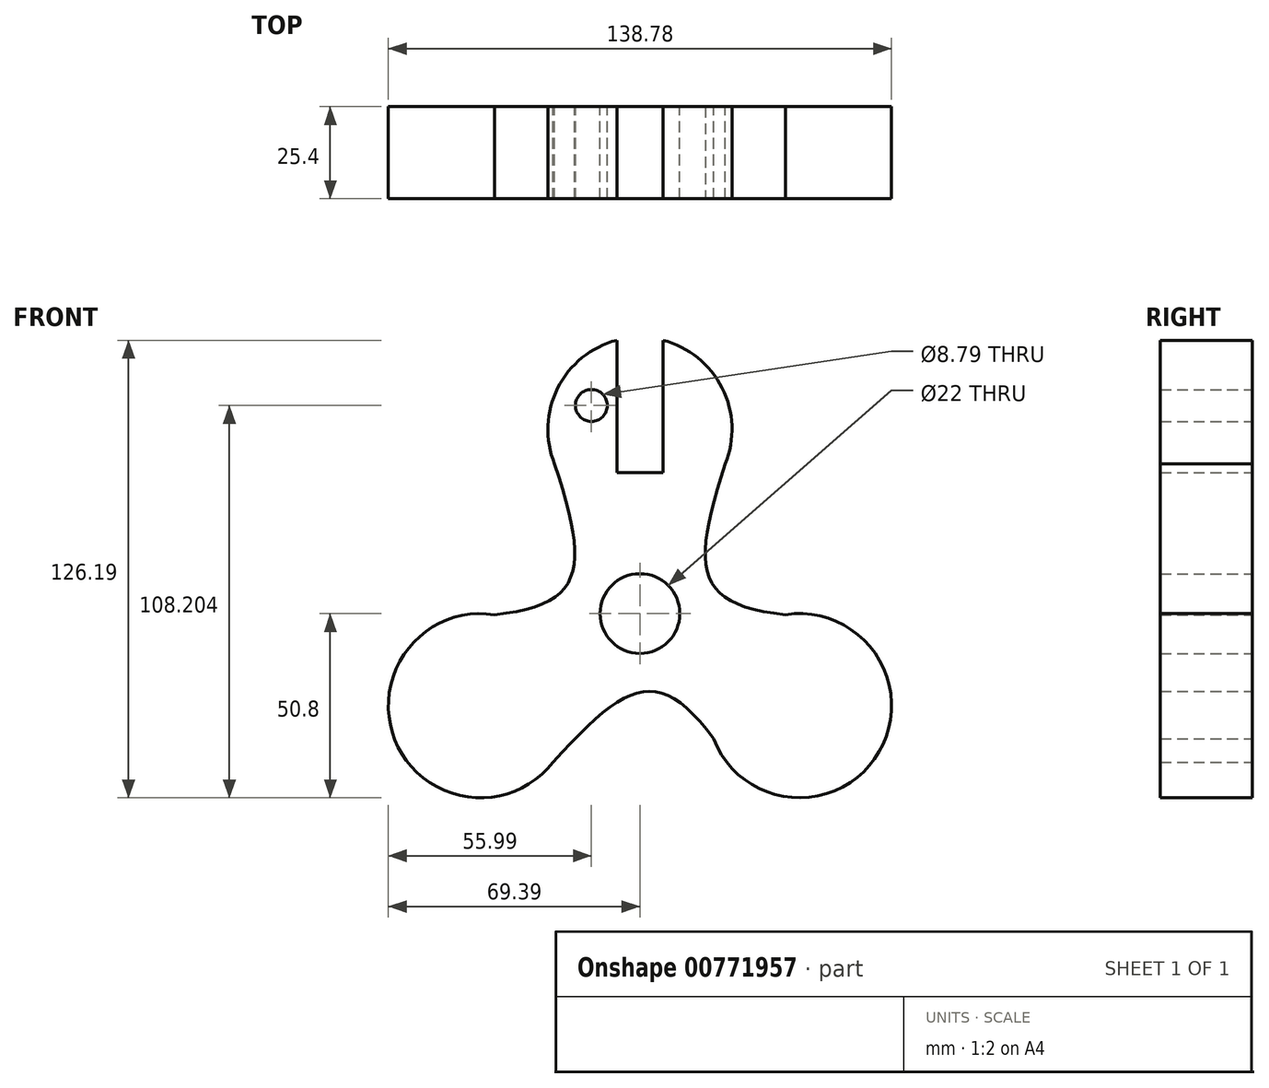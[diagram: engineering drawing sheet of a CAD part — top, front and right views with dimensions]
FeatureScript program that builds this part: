
annotation { "Feature Type Name" : "Feature", "Feature Type Description" : "" }
export const myFeature = defineFeature(function(context is Context, id is Id, definition is map)
    precondition{}
    {
        {
            var Q0;
            Q0=qCreatedBy(makeId("Front.planeOp"),FACE);
            var sketch = newSketch(context, id + "F0", { "sketchPlane" : qUnion([Q0])});
            skCircle(sketch, "E0", {"center": v(0, 0) * mm, "radius": 50.8 * mm, "construction": true});
            skCircle(sketch, "E1", {"center": v(0, 0) * mm, "radius": 11 * mm});
            skLineSegment(sketch, "E2", {"start": v(0, 0) * mm, "end": v(0, 50.8) * mm, "construction": true});
            skLineSegment(sketch, "E3", {"start": v(0, 0) * mm, "end": v(-44, -25.4) * mm, "construction": true});
            skLineSegment(sketch, "E4", {"start": v(0, 0) * mm, "end": v(44, -25.4) * mm, "construction": true});
            skArc(sketch, "E5", {"start": v(-6.35, 75.4) * mm, "mid": v(0, 25.4) * mm, "end": v(6.35, 75.4) * mm});
            skPoint(sketch, "E6.center", {"position": v(-0.18, 4.76) * mm});
            skLineSegment(sketch, "E7", {"start": v(0, 0) * mm, "end": v(38.5, 22.22) * mm, "construction": true});
            skLineSegment(sketch, "E8", {"start": v(0, 0) * mm, "end": v(0, -44.45) * mm, "construction": true});
            skLineSegment(sketch, "E9", {"start": v(0, 0) * mm, "end": v(-38.5, 22.22) * mm, "construction": true});
            skCircle(sketch, "E10", {"center": v(44, -25.4) * mm, "radius": 25.4 * mm});
            skCircle(sketch, "E11", {"center": v(-44, -25.4) * mm, "radius": 25.4 * mm});
            skLineSegment(sketch, "E12", {"start": v(-6.35, 75.4) * mm, "end": v(-6.35, 38.84) * mm});
            skLineSegment(sketch, "E13", {"start": v(0, 50.8) * mm, "end": v(0, 76.2) * mm, "construction": true});
            skLineSegment(sketch, "E14", {"start": v(6.35, 38.84) * mm, "end": v(6.35, 75.4) * mm});
            skLineSegment(sketch, "E15", {"start": v(-6.35, 38.84) * mm, "end": v(6.35, 38.84) * mm});
            skPoint(sketch, "E16.visualSharp", {"position": v(-38.5, 22.22) * mm});
            skPoint(sketch, "E17.visualSharp", {"position": v(38.5, 22.22) * mm});
            skPoint(sketch, "E18.visualSharp", {"position": v(0, -44.45) * mm});
            skLineSegment(sketch, "E19", {"start": v(-50.8, -0.93) * mm, "end": v(-50.8, -0.93) * mm});
            skLineSegment(sketch, "E20.2.0", {"start": v(24.6, 44.45) * mm, "end": v(24.6, 44.45) * mm});
            skArc(sketch, "E20.2.1", {"start": v(-24.6, 44.45) * mm, "mid": v(-23.62, 41.6) * mm, "end": v(-22.4, 38.84) * mm});
            skPoint(sketch, "E21", {"position": v(44, 0) * mm});
            skPoint(sketch, "E22.1.0", {"position": v(-22, 38.1) * mm});
            skPoint(sketch, "E22.2.0", {"position": v(-22, -38.1) * mm});
            skPoint(sketch, "E23", {"position": v(-50.8, -0.93) * mm});
            skPoint(sketch, "E24", {"position": v(24.6, 44.45) * mm});
            skPoint(sketch, "E25", {"position": v(26.2, -43.52) * mm});
            skPoint(sketch, "E26.start.orphan", {"position": v(55.46, 0) * mm});
            skPoint(sketch, "E27", {"position": v(-26.2, -43.52) * mm});
            skPoint(sketch, "E28.1.0", {"position": v(50.8, -0.93) * mm});
            skPoint(sketch, "E28.2.0", {"position": v(-24.6, 44.45) * mm});
            skLineSegment(sketch, "E29", {"start": v(-22, -12.7) * mm, "end": v(22, -12.7) * mm, "construction": true});
            skLineSegment(sketch, "E30", {"start": v(22, -12.7) * mm, "end": v(0, 25.4) * mm, "construction": true});
            skLineSegment(sketch, "E31", {"start": v(0, 25.4) * mm, "end": v(-22, -12.7) * mm, "construction": true});
            skFitSpline(sketch, "E32", {"points": [v(-26.2, -43.52) * mm, v(26.2, -43.52) * mm], "startDerivative": vector(72.18, 81.54) * mm, "endDerivative": vector(58.11, -95.1) * mm});
            skFitSpline(sketch, "E33.MirrorCS", {"points": [v(24.6, 44.45) * mm, v(50.8, -0.93) * mm], "startDerivative": vector(-34.52, -103.28) * mm, "endDerivative": vector(111.41, -2.78) * mm});
            skFitSpline(sketch, "E34.MirrorCS", {"points": [v(-24.6, 44.45) * mm, v(-50.8, -0.93) * mm], "startDerivative": vector(34.52, -103.28) * mm, "endDerivative": vector(-111.41, -2.78) * mm});
            skArc(sketch, "E35.trimOffspring", {"start": v(-26.2, -43.52) * mm, "mid": v(-24.21, -41.26) * mm, "end": v(-22.43, -38.82) * mm});
            skLineSegment(sketch, "E36.trimOffspring", {"start": v(50.8, -0.93) * mm, "end": v(50.8, -0.93) * mm});
            skCircle(sketch, "E37", {"center": v(-13.4, 57.4) * mm, "radius": 4.4 * mm});
            skSolve(sketch);
        }
        {
            var Q0;
            Q0 = qSketchRegion(id + "F0", true);
            extrude(context, id + "F1", {"entities" : qUnion([Q0]), "depth" : 25.4 * mm, "offsetDistance" : 25.4 * mm});
        }
    });
